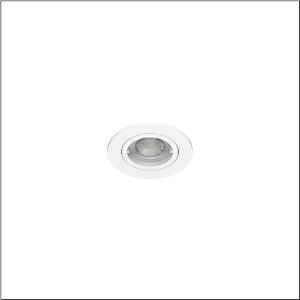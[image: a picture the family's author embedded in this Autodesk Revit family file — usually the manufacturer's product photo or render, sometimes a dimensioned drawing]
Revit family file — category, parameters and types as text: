
# Revit family: lunis_41_spot_51dt137a31a
name_source: partatom
category: Lighting Fixtures
units: mm (PartAtom-declared; Revit-internal decimal feet)

## family parameters
Cut with Voids When Loaded = No
Host = Face
Light Source = No
Part Type = Normal
Room Calculation Point = No
Round Connector Dimension = Use Diameter
Shared = No

## types (1)
- Lunis 41 Spot (1 x LED, 500 lm, 5 W, 3000K)
    Apparent Load = 5 VA
    CIE Flux Codes = 87 97 99 100 100
    Color Rendering = 80
    Color Temperature = 3000K
    Default Elevation = 1800 mm
    Description = Lunis 41,  Spot, downlight, light emission: direct distribution, LED rated luminous flux: 500lm, light colour: 830, control gear: ECG, mains connection: 230V, AC, 50/60Hz, housing, round, of aluminium, coated, traffic white (RAL 9016), diameter: 88mm, recess depth: 54mm, protection rating (complete): IP20, protection rating (on room side): IP20, insulation class (complete): insulation class II (safety insulation), certification: CE, permissible ambient temperature for indoor applications: -20..+40°C, packaging unit: 1 piece
    Height = 0 mm  [stored 0 ft]
    Lamp = 1 x LED
    Lamp Light Flux = 500 lm
    Lamp Power = 5 W
    Lamp count = 1
    Length = 88 mm
    Luminous efficacy = 100 lm/W
    Manufacturer = Siteco
    ModVariant = No
    Model = 51DT137A31A
    Mounting Place = Ceiling
    Mounting Type = Recessed
    Number of Poles = 1
    OnlyDefault = Yes
    Power Factor = 1
    Product Name = Lunis 41 Spot
    Product group = downlight
    ProductGroupID = 400
    Protection Class = Protection class II
    Protection Degree = IP 20
    RLX_Detail_Level = 1
    RLX_Emergency_Light_Flux = 0 lm
    RLX_Emergency_Type = 0
    RLX_Emergency_Type_DB = No
    RlxData = <blob elided: 37985 chars, md5=dcaf674a>
    Socket = socket
    Standby Power = 0 W
    System Light Flux = 500 lm
    System Power = 5 W
    Type Comments = Product without accessories
    Type Image = l_1005286.jpg
    URL = http://relux.com
    VarID = ---
    Voltage = 0 V
    Weight = 0.00 kg
    Width = 0 mm  [stored 0 ft]

note: [stored X ft] marks values corroborated as IEEE doubles in the binary element streams (Revit-internal decimal feet)

## geometry (parser evidence)
native form markers: Blend x4, Sweep x11
no freeform markers — native parametric forms only
